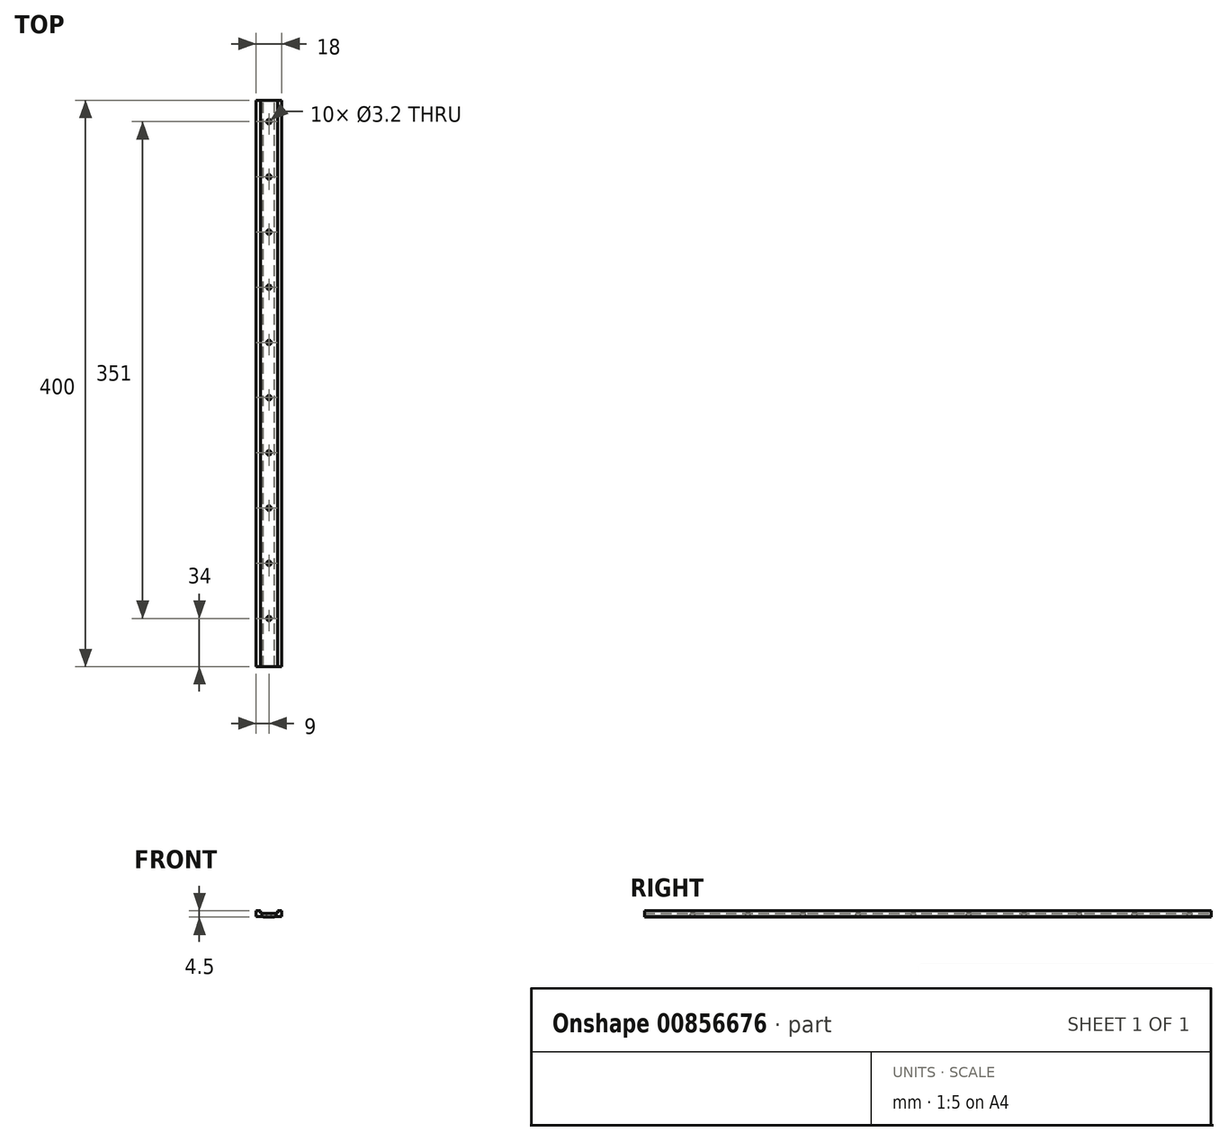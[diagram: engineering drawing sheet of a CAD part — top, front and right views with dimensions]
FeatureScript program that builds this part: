
annotation { "Feature Type Name" : "Feature", "Feature Type Description" : "" }
export const myFeature = defineFeature(function(context is Context, id is Id, definition is map)
    precondition{}
    {
        {
            var Q0;
            Q0=qCreatedBy(makeId("Front.planeOp"),FACE);
            var sketch = newSketch(context, id + "F0", { "sketchPlane" : qUnion([Q0])});
            skLineSegment(sketch, "E0", {"start": v(0, 29.45) * mm, "end": v(0, -27.17) * mm, "construction": true});
            skLineSegment(sketch, "E1", {"start": v(0, 0) * mm, "end": v(-6, 0) * mm});
            skLineSegment(sketch, "E2", {"start": v(-6, 0) * mm, "end": v(-6, 2) * mm});
            skLineSegment(sketch, "E3", {"start": v(-6, 2) * mm, "end": v(-9, 2) * mm});
            skLineSegment(sketch, "E4", {"start": v(-9, 2) * mm, "end": v(-9, -2) * mm});
            skLineSegment(sketch, "E5", {"start": v(-9, -2) * mm, "end": v(-4, -2) * mm});
            skLineSegment(sketch, "E6", {"start": v(-4, -2) * mm, "end": v(-4, -2.5) * mm});
            skLineSegment(sketch, "E7", {"start": v(-4, -2.5) * mm, "end": v(0, -2.5) * mm});
            skLineSegment(sketch, "E8.MirrorCS", {"start": v(4, -2) * mm, "end": v(4, -2.5) * mm});
            skLineSegment(sketch, "E9.MirrorCS", {"start": v(6, 0) * mm, "end": v(6, 2) * mm});
            skLineSegment(sketch, "E10.MirrorCS", {"start": v(4, -2.5) * mm, "end": v(0, -2.5) * mm});
            skLineSegment(sketch, "E11.MirrorCS", {"start": v(6, 2) * mm, "end": v(9, 2) * mm});
            skLineSegment(sketch, "E12.MirrorCS", {"start": v(9, -2) * mm, "end": v(4, -2) * mm});
            skLineSegment(sketch, "E13.MirrorCS", {"start": v(0, 0) * mm, "end": v(6, 0) * mm});
            skLineSegment(sketch, "E14.MirrorCS", {"start": v(9, 2) * mm, "end": v(9, -2) * mm});
            skSolve(sketch);
        }
        {
            var Q0;
            Q0=makeQuery(id+"F0.imprint","IMPRINT",FACE,{"disambiguationData":[TD([[makeQuery(id+"F0.imprint","IMPRINT",EDGE,{"derivedFrom":sQuery(id+"F0.wireOp",EDGE,"E1")}),1.0]])]});
            extrude(context, id + "F1", {"entities" : qUnion([Q0]), "depth" : 400 * mm, "offsetDistance" : 25 * mm});
        }
        {
            var Q0;
            Q0=makeQuery(id+"F1.opExtrude","SWEPT_FACE",FACE,{"disambiguationData":[OSD([sQuery(id+"F0.wireOp",EDGE,"E1"),sQuery(id+"F0.wireOp",EDGE,"E13.MirrorCS")])]});
            var sketch = newSketch(context, id + "F2", { "sketchPlane" : qUnion([Q0])});
            skCircle(sketch, "E15", {"center": v(0, -15) * mm, "radius": 1.6 * mm});
            skCircle(sketch, "E16.0.1.0", {"center": v(0, -54) * mm, "radius": 1.6 * mm});
            skCircle(sketch, "E16.0.2.0", {"center": v(0, -93) * mm, "radius": 1.6 * mm});
            skCircle(sketch, "E16.0.3.0", {"center": v(0, -132) * mm, "radius": 1.6 * mm});
            skCircle(sketch, "E16.0.4.0", {"center": v(0, -171) * mm, "radius": 1.6 * mm});
            skCircle(sketch, "E16.0.5.0", {"center": v(0, -210) * mm, "radius": 1.6 * mm});
            skCircle(sketch, "E16.0.6.0", {"center": v(0, -249) * mm, "radius": 1.6 * mm});
            skCircle(sketch, "E16.0.7.0", {"center": v(0, -288) * mm, "radius": 1.6 * mm});
            skCircle(sketch, "E16.0.8.0", {"center": v(0, -327) * mm, "radius": 1.6 * mm});
            skCircle(sketch, "E16.0.9.0", {"center": v(0, -366) * mm, "radius": 1.6 * mm});
            skLineSegment(sketch, "E16.direction1", {"start": v(0, -15) * mm, "end": v(25, -15) * mm, "construction": true});
            skLineSegment(sketch, "E16.direction2", {"start": v(0, -15) * mm, "end": v(0, -54) * mm, "construction": true});
            skSolve(sketch);
        }
        {
            var Q0;
            Q0 = qSketchRegion(id + "F2", true);
            extrude(context, id + "F3", {"entities" : qUnion([Q0]), "operationType" : NewBodyOperationType.REMOVE, "oppositeDirection" : true, "depth" : 25 * mm, "offsetDistance" : 25 * mm});
        }
    });
